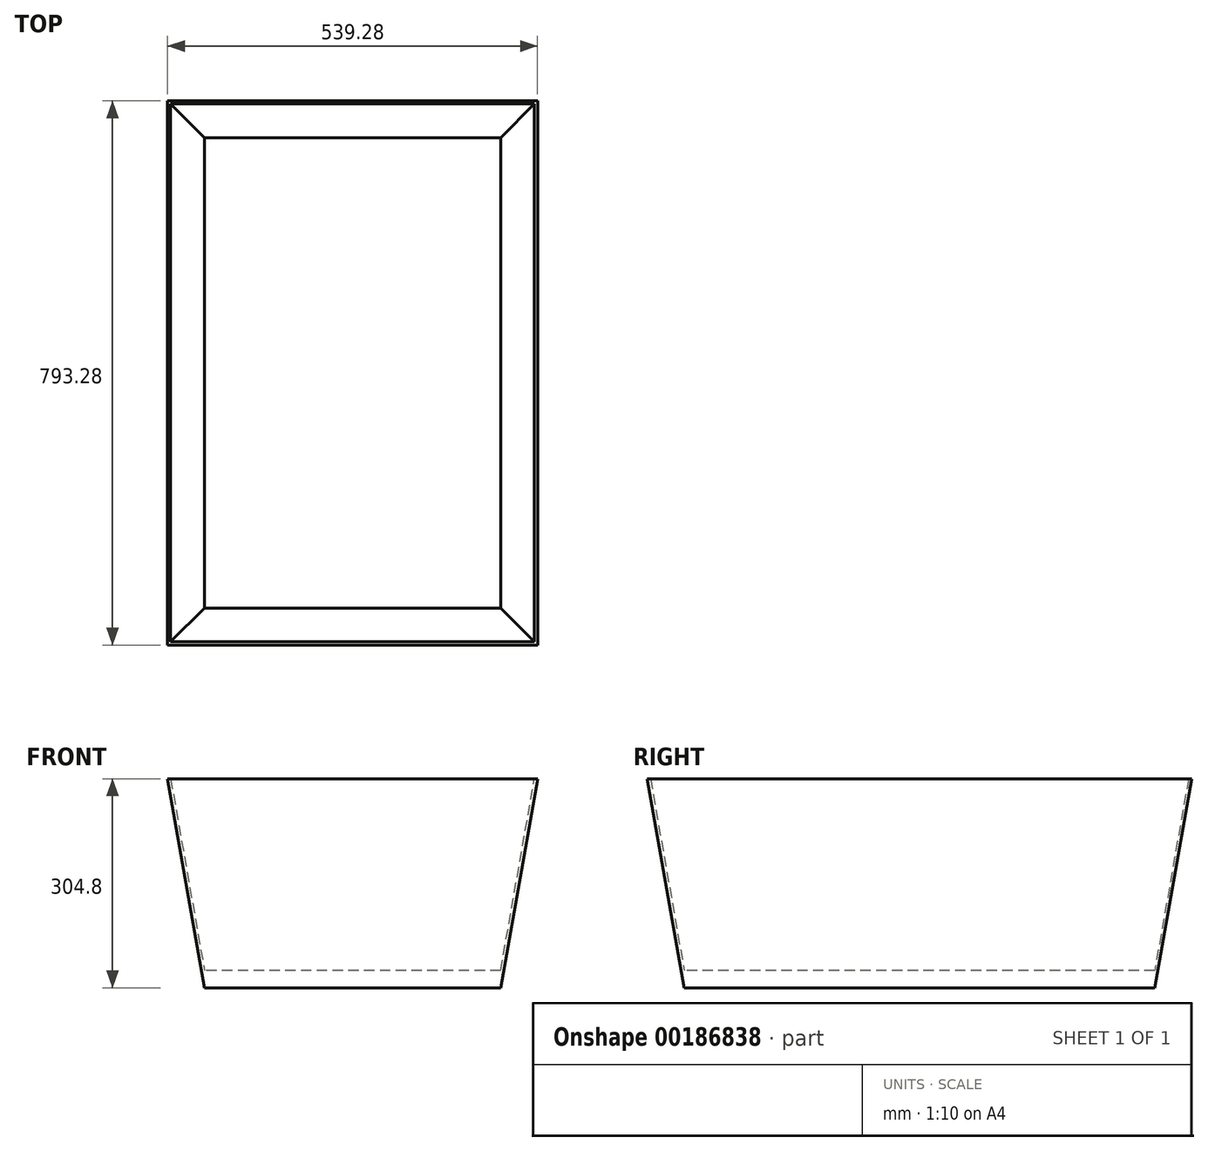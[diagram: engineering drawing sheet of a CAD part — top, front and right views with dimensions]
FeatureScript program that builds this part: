
annotation { "Feature Type Name" : "Feature", "Feature Type Description" : "" }
export const myFeature = defineFeature(function(context is Context, id is Id, definition is map)
    precondition{}
    {
        {
            var Q0;
            Q0=qCreatedBy(makeId("Top.planeOp"),FACE);
            var sketch = newSketch(context, id + "F0", { "sketchPlane" : qUnion([Q0])});
            skLineSegment(sketch, "E0.bottom", {"start": v(215.9, 342.9) * mm, "end": v(-215.9, 342.9) * mm});
            skLineSegment(sketch, "E0.top", {"start": v(215.9, -342.9) * mm, "end": v(-215.9, -342.9) * mm});
            skLineSegment(sketch, "E0.left", {"start": v(215.9, 342.9) * mm, "end": v(215.9, -342.9) * mm});
            skLineSegment(sketch, "E0.right", {"start": v(-215.9, 342.9) * mm, "end": v(-215.9, -342.9) * mm});
            skPoint(sketch, "E0.middle", {"position": v(0, 0) * mm});
            skSolve(sketch);
        }
        {
            var Q0;
            Q0 = qSketchRegion(id + "F0", true);
            extrude(context, id + "F1", {"entities" : qUnion([Q0]), "depth" : 304.8 * mm, "hasDraft" : true, "draftAngle" : 10 * degree});
        }
        {
            var Q0;
            Q0=qCreatedBy(makeId("Top.planeOp"),FACE);
            cPlane(context, id + "F2", {"entities" : qUnion([Q0]), "cplaneType" : CPlaneType.OFFSET, "offset" : 25.4 * mm, "width" : 152.4 * mm, "height" : 152.4 * mm});
        }
        {
            var Q0;
            Q0=qCreatedBy(id+"F2.planeOp",FACE);
            var sketch = newSketch(context, id + "F3", { "sketchPlane" : qUnion([Q0])});
            skLineSegment(sketch, "E1.bottom", {"start": v(215.9, -342.9) * mm, "end": v(-215.9, -342.9) * mm});
            skLineSegment(sketch, "E1.top", {"start": v(215.9, 342.9) * mm, "end": v(-215.9, 342.9) * mm});
            skLineSegment(sketch, "E1.left", {"start": v(215.9, -342.9) * mm, "end": v(215.9, 342.9) * mm});
            skLineSegment(sketch, "E1.right", {"start": v(-215.9, -342.9) * mm, "end": v(-215.9, 342.9) * mm});
            skPoint(sketch, "E1.middle", {"position": v(0, 0) * mm});
            skSolve(sketch);
        }
        {
            var Q0;
            Q0 = qSketchRegion(id + "F3", true);
            extrude(context, id + "F4", {"entities" : qUnion([Q0]), "operationType" : NewBodyOperationType.REMOVE, "depth" : 279.4 * mm, "hasDraft" : true, "draftAngle" : 10 * degree});
        }
    });
